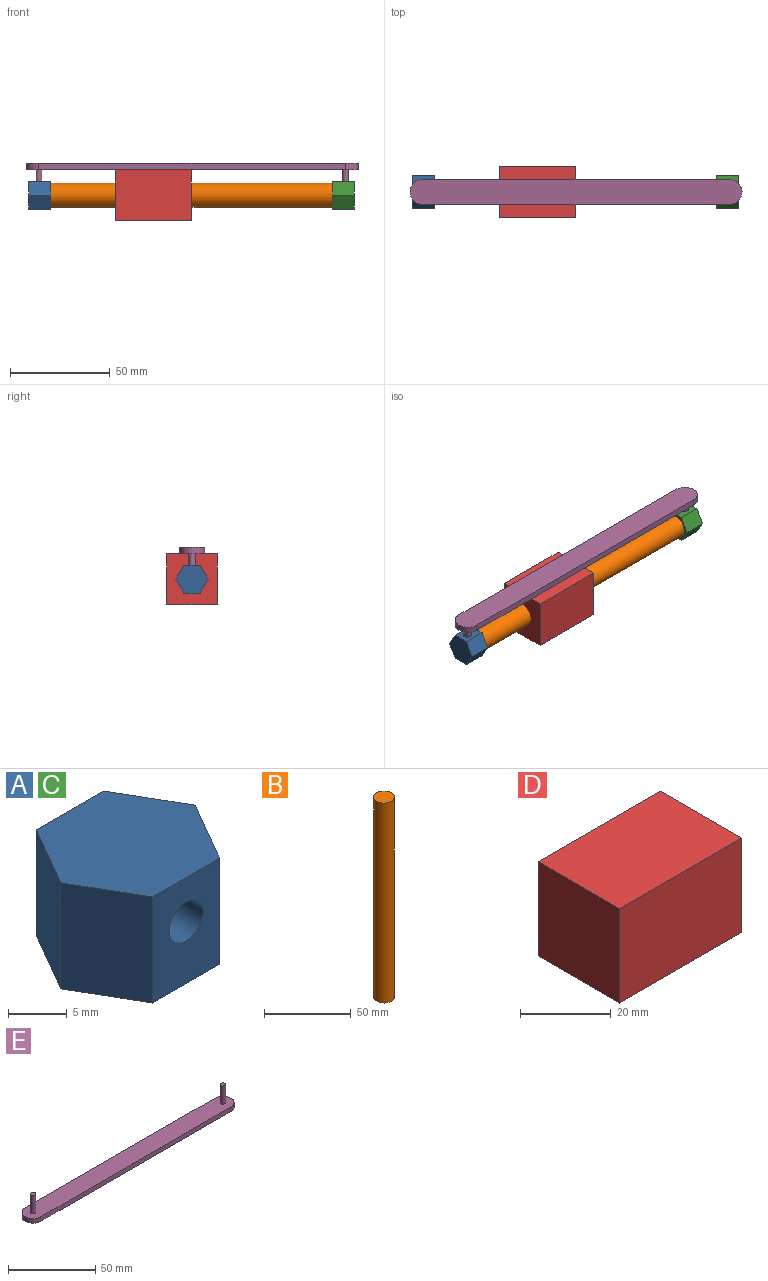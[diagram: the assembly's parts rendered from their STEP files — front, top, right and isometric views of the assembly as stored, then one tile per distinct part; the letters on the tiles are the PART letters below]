
ASSEMBLY  parts=5 mates=6
PART A: 10 faces, bbox 16.2x14x11 mm
  f0: plane 11.05x7.01mm, normal (0.87,0.5,0), area 89.4mm2, adj f1,f5,f6,f7
  f1: plane 11.05x8.1mm, normal (0,1,0), area 89.4mm2, adj f0,f2,f6,f7
  f2: plane 11.05x7.01mm, normal (-0.87,0.5,0), area 89.4mm2, adj f1,f3,f6,f7
  f3: plane 11.05x7.01mm, normal (-0.87,-0.5,0), area 89.4mm2, adj f2,f4,f6,f7
  f4: plane 11.05x8.1mm, normal (0,-1,0), area 76.5mm2, adj f3,f5,f6,f7,f8
  f5: plane 11.05x7.01mm, normal (0.87,-0.5,0), area 89.4mm2, adj f0,f4,f6,f7
  f6: plane 16.19x14.02mm, normal (0,0,1), area 170.2mm2, adj f0,f1,f2,f3,f4,f5
  f7: plane 16.19x14.02mm, normal (0,0,-1), area 170.2mm2, adj f0,f1,f2,f3,f4,f5
  f8: cylinder r=2.03mm len=9.04mm, axis (0,-1,0), area 115.4mm2, adj f4,f9
  f9: plane 4.06x4.06mm, normal (0,-1,0), area 13mm2, adj f8
PART B: 3 faces, bbox 12.1x12.1x141.2 mm
  f0: cylinder r=6.03mm len=141.22mm, axis (0,0,-1), area 5352.9mm2, adj f1,f2
  f1: plane 12.07x12.07mm, normal (0,0,1), area 114.3mm2, adj f0
  f2: plane 12.07x12.07mm, normal (0,0,-1), area 114.3mm2, adj f0
PART C: same geometry as A
PART D: 6 faces, bbox 38.1x25.4x25.4 mm
  f0: plane 25.4x25.4mm, normal (1,0,0), area 645.2mm2, adj f1,f3,f4,f5
  f1: plane 38.1x25.4mm, normal (0,1,0), area 967.7mm2, adj f0,f2,f4,f5
  f2: plane 25.4x25.4mm, normal (-1,0,0), area 645.2mm2, adj f1,f3,f4,f5
  f3: plane 38.1x25.4mm, normal (0,-1,0), area 967.7mm2, adj f0,f2,f4,f5
  f4: plane 38.1x25.4mm, normal (0,0,1), area 967.7mm2, adj f0,f1,f2,f3
  f5: plane 38.1x25.4mm, normal (0,0,-1), area 967.7mm2, adj f0,f1,f2,f3
PART E: 10 faces, bbox 166.4x12.7x15.9 mm
  f0: plane 153.67x3.18mm, normal (0,1,0), area 487.9mm2, adj f2,f3,f8,f9
  f1: plane 153.67x3.18mm, normal (0,-1,0), area 487.9mm2, adj f2,f3,f8,f9
  f2: plane 166.37x12.7mm, normal (0,0,1), area 2062.5mm2, adj f0,f1,f4,f6,f8,f9
  f3: plane 166.37x12.7mm, normal (0,0,-1), area 2078.3mm2, adj f0,f1,f8,f9
  f4: cylinder r=1.59mm len=12.7mm, axis (0,0,-1), area 126.7mm2, adj f2,f5
  f5: plane 3.18x3.18mm, normal (0,0,1), area 7.9mm2, adj f4
  f6: cylinder r=1.59mm len=12.7mm, axis (0,0,-1), area 126.7mm2, adj f2,f7
  f7: plane 3.18x3.18mm, normal (0,0,1), area 7.9mm2, adj f6
  f8: cylinder r=6.35mm len=12.7mm, axis (0,0,-1), area 63.3mm2, adj f0,f1,f2,f3
  f9: cylinder r=6.35mm len=12.7mm, axis (0,0,-1), area 63.3mm2, adj f0,f1,f2,f3
PLACE A rot(axis=(-0.58,-0.58,0.58),120deg) t=(-51.56,0,12.7)mm
PLACE B rot(axis=(0,-1,0),90deg) t=(89.66,0,12.7)mm
PLACE C rot(axis=(-0.58,0.58,-0.58),120deg) t=(89.66,0,12.7)mm
PLACE D at identity fixed
PLACE E rot(axis=(1,0,0),180deg) t=(19.3,0,28.58)mm
MATE fastened A.f7 <-> B.f0  axis (1,0,0) through (-51.56,0,12.7)mm
MATE fastened C.f7 <-> B.f0  axis (-1,0,0) through (89.66,0,12.7)mm
MATE planar E.f2 <-> D.f4  axis (0,0,-1) through (19.3,0,25.4)mm
MATE parallel E.f0 <-> D.f3  axis (0,-1,0) through (19.3,-6.35,26.99)mm
MATE fastened B.f0 <-> D.f0  axis (1,0,0) through (19.05,0,12.7)mm
MATE cylindrical E.f6 <-> C.f8  axis (0,0,-1) through (96.14,0,25.4)mm
